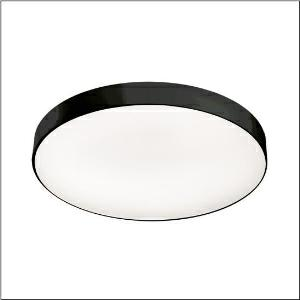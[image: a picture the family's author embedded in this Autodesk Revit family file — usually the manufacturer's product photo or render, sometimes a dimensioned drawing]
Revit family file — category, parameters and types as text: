
# Revit family: round_21_l_51mr38nd0321b
name_source: partatom
category: Lighting Fixtures
units: mm (PartAtom-declared; Revit-internal decimal feet)

## family parameters
Cut with Voids When Loaded = No
Host = Face
Light Source = No
Part Type = Normal
Room Calculation Point = No
Round Connector Dimension = Use Diameter
Shared = No

## types (1)
- Round 21 L (1 x LED, 11740 lm, 88.2 W, 3000K)
    Apparent Load = 88 VA
    CIE Flux Codes = 66 90 98 71 100
    Color Rendering = 80
    Color Temperature = 3000K
    Default Elevation = 1800 mm
    Description = Round 21 L, wall and ceiling luminaire, primary optical cover: micro prismatic cover, of PMMA, transparent, CAT 2 (L<= 3000cd/m²), light emission: direct/indirect distribution, primary light characteristic: symmetric, installation type: suspended mounting, surface-mounted, LED, rated luminous flux: 9.230lm, luminous efficacy: 111lm/W, light colour: 830, colour temperature: 3000K, with terminal, 5-pole, mains connection: 230V, AC, 50/60Hz, rated input power: 83W, housing, of aluminium, coated, black, diameter: 850mm, height: 62mm, protection rating (complete): IP40, insulation class (complete): insulation class I (protective earthing), certification: CE, impact resistance: IK04, permissible operating ambient temperature: -10..+35°C, packaging unit: 1 piece
    Height = 87 mm
    Lamp = 1 x LED
    Lamp Light Flux = 11740 lm
    Lamp Power = 88.2 W
    Lamp count = 1
    Length = 850 mm
    Luminous efficacy = 133 lm/W
    Manufacturer = Siteco
    ModVariant = No
    Model = 51MR38ND0321B
    Mounting Place = Ceiling
    Mounting Type = Surface mounted
    Number of Poles = 1
    OnlyDefault = Yes
    Power Factor = 1
    Product Name = Round 21 L
    Product group = wall and ceiling luminaire
    ProductGroupID = 303
    Protection Class = Protection class I
    Protection Degree = IP 40
    RLX_Detail_Level = 1
    RLX_Emergency_Light_Flux = 0 lm
    RLX_Emergency_Type = 0
    RLX_Emergency_Type_DB = No
    RlxData = <blob elided: 28645 chars, md5=5161f033>
    Socket = socket
    Standby Power = 0 W
    System Light Flux = 11740 lm
    System Power = 88 W
    Type Comments = Product without accessories
    Type Image = l_1258326.jpg
    URL = http://relux.com
    VarID = ---
    Voltage = 0 V
    Weight = 0.00 kg
    Width = 0 mm  [stored 0 ft]

note: [stored X ft] marks values corroborated as IEEE doubles in the binary element streams (Revit-internal decimal feet)

## geometry (parser evidence)
native form markers: Blend x4, Sweep x11
no freeform markers — native parametric forms only
